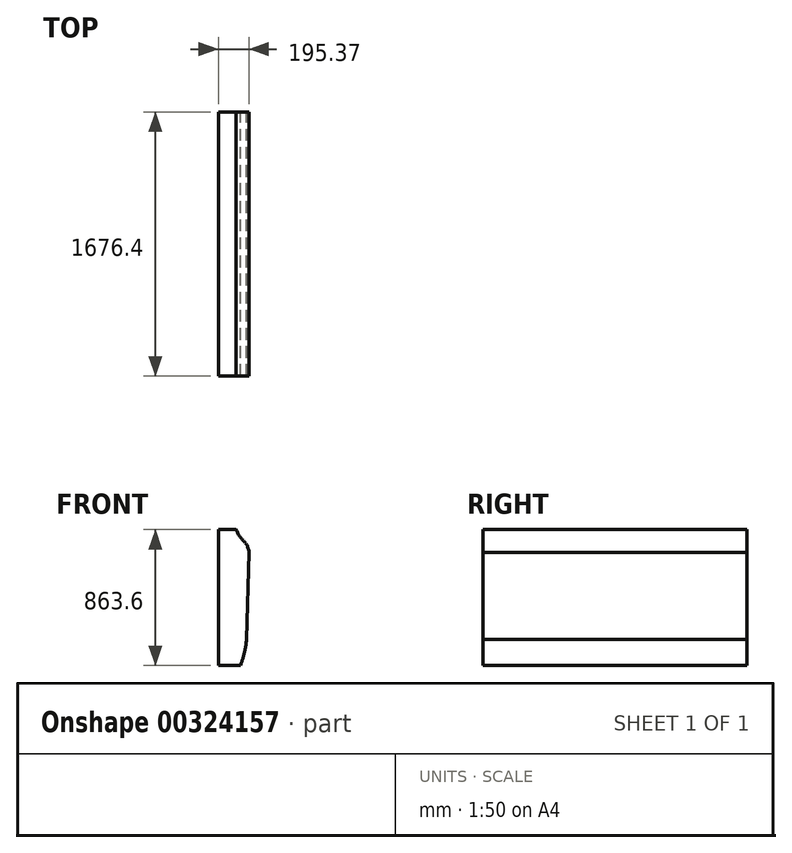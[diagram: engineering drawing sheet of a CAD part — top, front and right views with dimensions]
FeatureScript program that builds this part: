
annotation { "Feature Type Name" : "Feature", "Feature Type Description" : "" }
export const myFeature = defineFeature(function(context is Context, id is Id, definition is map)
    precondition{}
    {
        {
            var Q0;
            Q0=qCreatedBy(makeId("Right.planeOp"),FACE);
            var sketch = newSketch(context, id + "F0", { "sketchPlane" : qUnion([Q0])});
            skLineSegment(sketch, "E0.top", {"start": v(757.37, 430.6) * mm, "end": v(-839.01, 430.6) * mm});
            skLineSegment(sketch, "E0.left", {"start": v(839.01, -430.6) * mm, "end": v(839.01, 295.38) * mm});
            skLineSegment(sketch, "E0.right", {"start": v(-839.01, -430.6) * mm, "end": v(-839.01, 430.6) * mm});
            skPoint(sketch, "E0.middle", {"position": v(0, 0) * mm});
            skFitSpline(sketch, "E1", {"points": [v(757.37, 430.6) * mm, v(839.01, 295.38) * mm], "startDerivative": vector(49.2, -65.86) * mm, "endDerivative": vector(0, -219.37) * mm});
            skFitSpline(sketch, "E2", {"points": [v(737.4, -426.72) * mm, v(839.01, -323.76) * mm], "startDerivative": vector(178.43, 0) * mm, "endDerivative": vector(31.45, 222.74) * mm});
            skArc(sketch, "E3", {"start": v(66.14, -367.6) * mm, "mid": v(-252.28, -122.54) * mm, "end": v(-536.97, -406.08) * mm});
            skLineSegment(sketch, "E4.top", {"start": v(-601.48, -456) * mm, "end": v(-839.01, -456) * mm});
            skLineSegment(sketch, "E4.right", {"start": v(-839.01, -430.6) * mm, "end": v(-839.01, -456) * mm});
            skLineSegment(sketch, "E5", {"start": v(163.35, -426.72) * mm, "end": v(737.4, -426.72) * mm});
            skPoint(sketch, "E6.orphan", {"position": v(839.01, 430.6) * mm});
            skFitSpline(sketch, "E7", {"points": [v(63.61, -356) * mm, v(163.35, -426.72) * mm], "startDerivative": vector(23.55, -161.35) * mm, "endDerivative": vector(117.99, 0) * mm});
            skFitSpline(sketch, "E8", {"points": [v(-601.48, -456) * mm, v(-536.97, -406.08) * mm], "startDerivative": vector(118, 2.67) * mm, "endDerivative": vector(14.48, 110.94) * mm});
            skSolve(sketch);
        }
        {
            var Q0;
            Q0=makeQuery(id+"F0.imprint","IMPRINT",FACE,{"disambiguationData":[TD([[makeQuery(id+"F0.imprint","IMPRINT",EDGE,{"derivedFrom":sQuery(id+"F0.wireOp",EDGE,"E0.top")}),1.0]])]});
            extrude(context, id + "F1", {"entities" : qUnion([Q0]), "depth" : 177.8 * mm});
        }
        {
            var Q0;
            Q0=makeQuery(id+"F1.opExtrude","CAP_EDGE",EDGE,{"disambiguationData":[OSD([sQuery(id+"F0.wireOp",EDGE,"E0.left")])],"isStart":false});
            fillet(context, id + "F2", {"entities" : qUnion([Q0]), "radius" : 50.8 * mm, "tangentPropagation" : true, "allowEdgeOverflow" : false});
        }
        {
            var Q0;
            Q0=makeQuery(id+"F1.opExtrude","SWEPT_FACE",FACE,{"disambiguationData":[OSD([sQuery(id+"F0.wireOp",EDGE,"E0.left")])]});
            var sketch = newSketch(context, id + "F3", { "sketchPlane" : qUnion([Q0])});
            skLineSegment(sketch, "E9.bottom", {"start": v(228.43, 421.25) * mm, "end": v(342.28, 421.25) * mm});
            skLineSegment(sketch, "E9.top", {"start": v(201.61, -442.35) * mm, "end": v(342.28, -442.35) * mm});
            skLineSegment(sketch, "E9.right", {"start": v(342.28, 421.25) * mm, "end": v(342.28, -442.35) * mm});
            skFitSpline(sketch, "E10", {"points": [v(228.43, 421.25) * mm, v(146.91, 274.73) * mm], "startDerivative": vector(-83.66, -236.82) * mm, "endDerivative": vector(-31.68, -241.32) * mm});
            skLineSegment(sketch, "E11", {"start": v(146.91, 274.73) * mm, "end": v(162.61, -277.6) * mm});
            skFitSpline(sketch, "E12", {"points": [v(162.61, -277.6) * mm, v(201.61, -442.35) * mm], "startDerivative": vector(23.7, -228.5) * mm, "endDerivative": vector(54.7, -153.17) * mm});
            skSolve(sketch);
        }
        {
            var Q0;
            Q0=makeQuery(id+"F3.imprint","IMPRINT",FACE,{"disambiguationData":[TD([[makeQuery(id+"F3.imprint","IMPRINT",EDGE,{"derivedFrom":sQuery(id+"F3.wireOp",EDGE,"E9.bottom")}),-1.0]])]});
            extrude(context, id + "F4", {"entities" : qUnion([Q0]), "oppositeDirection" : true, "depth" : 1676.4 * mm});
        }
        {
            var Q0;
            Q0=makeQuery(id+"F1.opExtrude","SWEPT_BODY",BODY,{"disambiguationData":[OSD([sQuery(id+"F0.wireOp",EDGE,"E0.top"),sQuery(id+"F0.wireOp",EDGE,"E0.left"),sQuery(id+"F0.wireOp",EDGE,"E0.right"),sQuery(id+"F0.wireOp",EDGE,"E1"),sQuery(id+"F0.wireOp",EDGE,"E2"),sQuery(id+"F0.wireOp",EDGE,"E3"),sQuery(id+"F0.wireOp",EDGE,"E4.top"),sQuery(id+"F0.wireOp",EDGE,"E4.right"),sQuery(id+"F0.wireOp",EDGE,"E5"),sQuery(id+"F0.wireOp",EDGE,"E7"),sQuery(id+"F0.wireOp",EDGE,"E8")])]});
            deleteBodies(context, id + "F5", {"entities" : qUnion([Q0])});
        }
    });
